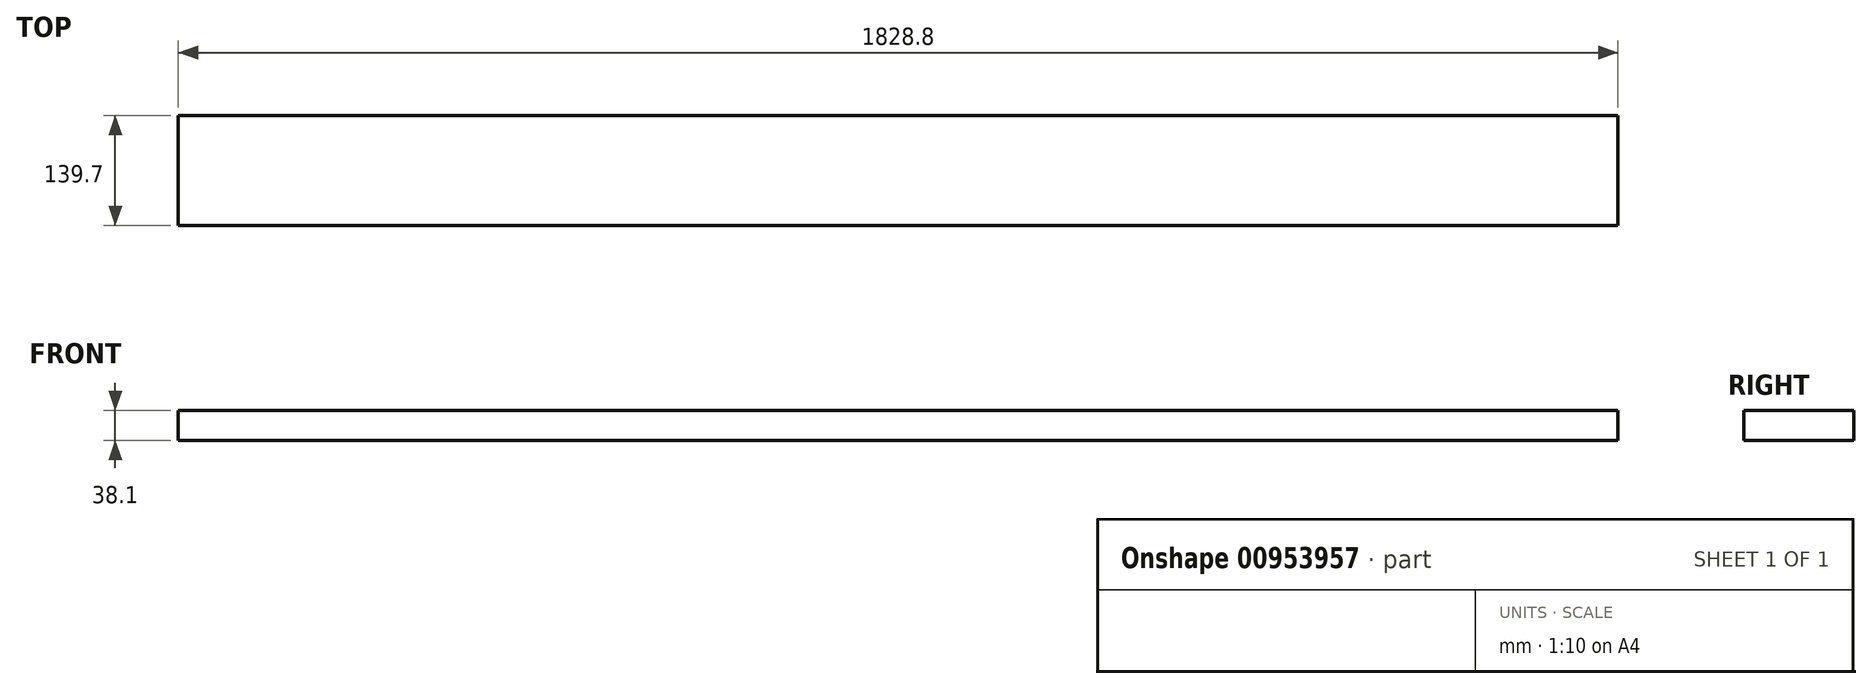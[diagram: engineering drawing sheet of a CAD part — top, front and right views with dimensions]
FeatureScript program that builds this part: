
annotation { "Feature Type Name" : "Feature", "Feature Type Description" : "" }
export const myFeature = defineFeature(function(context is Context, id is Id, definition is map)
    precondition{}
    {
        {
            var Q0;
            Q0=qCreatedBy(makeId("Top.planeOp"),FACE);
            var sketch = newSketch(context, id + "F0", { "sketchPlane" : qUnion([Q0])});
            skLineSegment(sketch, "E0.bottom", {"start": v(0, 0) * mm, "end": v(1828.8, 0) * mm});
            skLineSegment(sketch, "E0.top", {"start": v(0, 139.7) * mm, "end": v(1828.8, 139.7) * mm});
            skLineSegment(sketch, "E0.left", {"start": v(0, 0) * mm, "end": v(0, 139.7) * mm});
            skLineSegment(sketch, "E0.right", {"start": v(1828.8, 0) * mm, "end": v(1828.8, 139.7) * mm});
            skSolve(sketch);
        }
        {
            var Q0;
            Q0=qSketchRegion(id+"F0",true);
            extrude(context, id + "F1", {"entities" : qUnion([Q0]), "depth" : 38.1 * mm, "offsetDistance" : 25.4 * mm});
        }
    });
